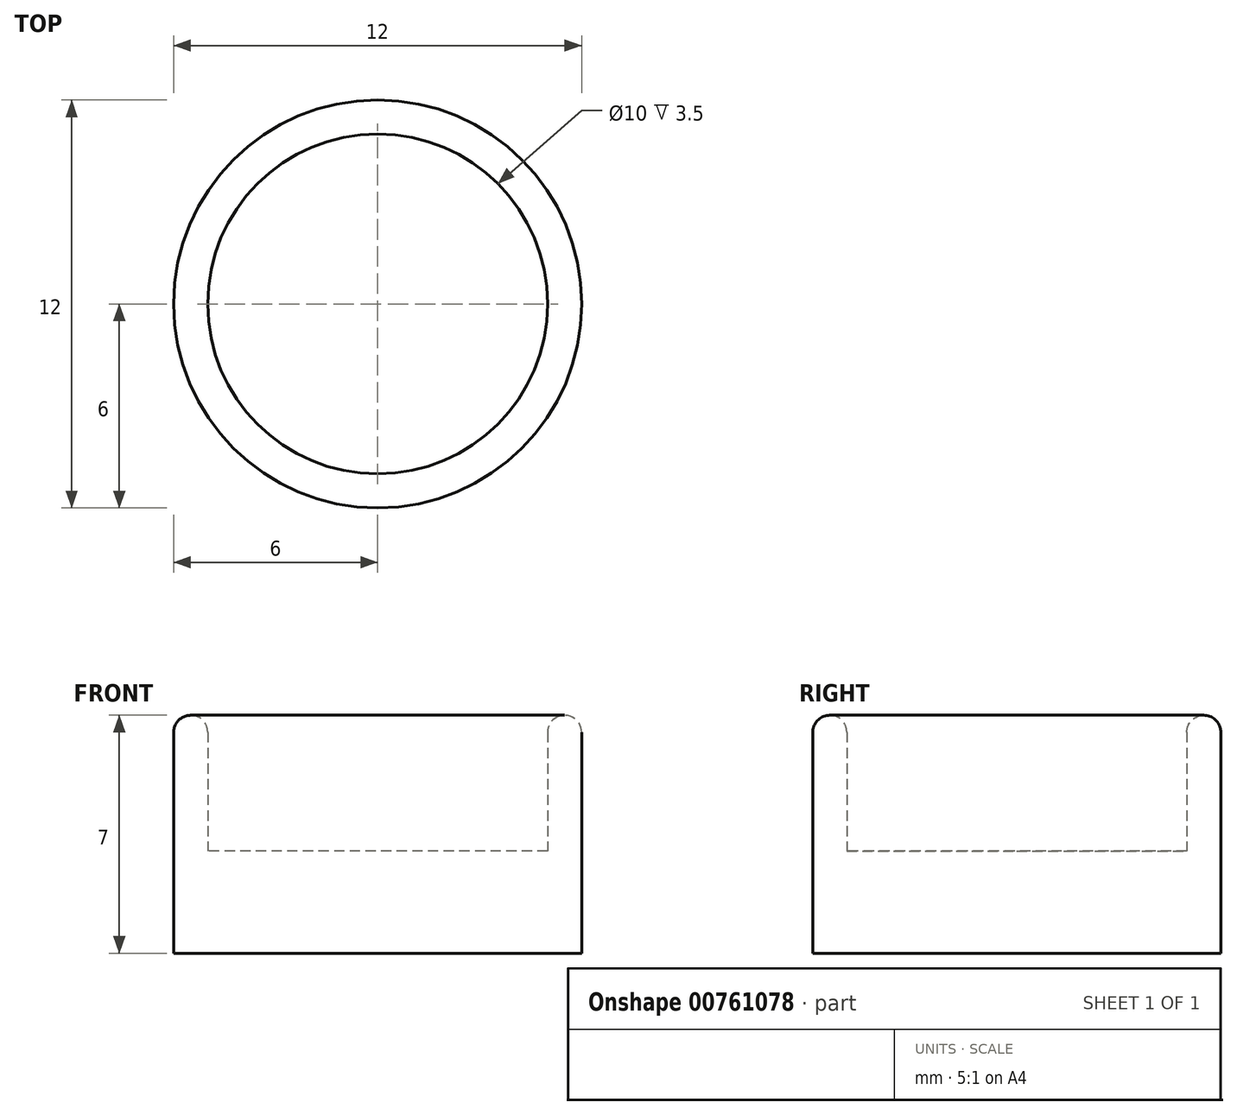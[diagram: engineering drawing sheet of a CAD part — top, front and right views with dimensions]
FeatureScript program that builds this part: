
annotation { "Feature Type Name" : "Feature", "Feature Type Description" : "" }
export const myFeature = defineFeature(function(context is Context, id is Id, definition is map)
    precondition{}
    {
        {
            var Q0;
            Q0=qCreatedBy(makeId("Top.planeOp"),FACE);
            var sketch = newSketch(context, id + "F0", { "sketchPlane" : qUnion([Q0])});
            skCircle(sketch, "E0", {"center": v(0, 0) * mm, "radius": 5 * mm});
            skCircle(sketch, "E1", {"center": v(0, 0) * mm, "radius": 6 * mm});
            skSolve(sketch);
        }
        {
            var Q0;
            Q0 = qSketchRegion(id + "F0", true);
            extrude(context, id + "F1", {"entities" : qUnion([Q0]), "depth" : 7 * mm, "offsetDistance" : 25 * mm});
        }
        {
            var Q0;
            Q0=makeQuery(id+"F0.imprint","IMPRINT",FACE,{"disambiguationData":[TD([[makeQuery(id+"F0.imprint","IMPRINT",EDGE,{"derivedFrom":sQuery(id+"F0.wireOp",EDGE,"E0")}),1.0]])]});
            extrude(context, id + "F2", {"entities" : qUnion([Q0]), "operationType" : NewBodyOperationType.ADD, "depth" : 3 * mm, "offsetDistance" : 25 * mm});
        }
        {
            var Q0;
            Q0=makeQuery(id+"F1.opExtrude","CAP_FACE",FACE,{"disambiguationData":[OSD([sQuery(id+"F0.wireOp",EDGE,"E0"),sQuery(id+"F0.wireOp",EDGE,"E1")])],"isStart":false});
            fillet(context, id + "F3", {"entities" : qUnion([Q0]), "radius" : 0.5 * mm, "tangentPropagation" : true, "allowEdgeOverflow" : false});
        }
    });
